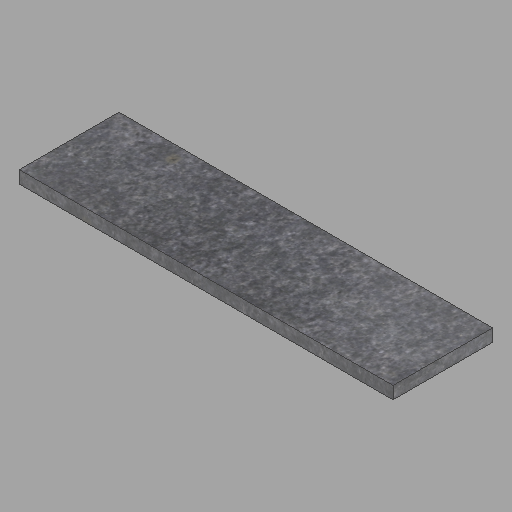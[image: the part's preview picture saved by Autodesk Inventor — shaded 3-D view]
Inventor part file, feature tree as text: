
AUTODESK INVENTOR PART (.ipt)
format: ipt  version: 2023 (Build 270158000, 158)  size: 192,000 bytes
history: native  units: in
note: dims shown in document units (in); Inventor stores cm internally (conversion verified against a paired STEP export)
features: other x1, extrude x1, sketch x1
ambient origin geometry x8: Origin, YZ Plane, XZ Plane, XY Plane, X Axis, Y Axis, Z Axis, Center Point
bodies: Solid1 (feature_tree)
feature tree (3):
  other  "2x16x60-6"
  extrude  "Extrusion1"  Depth=16.0in
  sketch  "Sketch1"  dims[d0=2.0in d1=16.0in d2=60.0in d3=0.0in]
